# Revit family: Drinking_Fountain-Pedestal_Mounted-Murdock_Mfg-GRF_Series.rfaxxx.xxx
name_source: partatom
category: Plumbing Fixtures
units: mm (PartAtom-declared; Revit-internal decimal feet)

## family parameters
Cut with Voids When Loaded = No
Host = Face
OmniClass Number = 23.65.70.14.11
OmniClass Title = Drinking Fountains/Coolers
Part Type = Normal
Room Calculation Point = No
Round Connector Dimension = Use Diameter
Shared = Yes

## types (4) — shared parameters
-CH30 Child height, 30" bubbler height = No
-FRU1 - Underground Freeze-Resistant Valve for One Pushbutton = No
-FRU2 Freeze resistant, 2 valves = No
-FRU3 Freeze resistant, 3 valves = No
-FS Foot spray = No
-HB1 Hose bibb, compression, with hose threaded outlet/VB = No
-HB2 Hose bibb, loose key, with hose threaded outlet/VB = No
-HB3 Hose bibb, loose key, vandal resistant,  with hose threaded outlet/VB = No
-IGM In-ground 14" mounting = No
-JF1 Jug filler, spigot, self-closing valve with plain end = No
-JF2 Jug filler, pushbutton, self-closing valve with plain end = No
-NP1 Non-pollutable, freeze resistant, 1 valve = No
-NP2 Non-pollutable, freeze resistant, 2 valves = No
-NP3 Non-pollutable, freeze resistant, 3 valves = No
-PF Pet fountain receptor = No
ADA Compliant = Yes
Activation = Push Button
Assembly Code = D2010810
CW Connection = Yes
CWFU = 1.5
Cold Water Connection Diameter = 1/4"
Compliance Certifications = NSF/ANSI 61, Section 9, Public Law 111-380 (NO-LEAD), and CHSC 116875
Default Elevation = 0"
Description = Round Stainless Steel Pedestal Drinking Fountain
Finish- Bubbler = Stainless Steel-Murdock-Polished
Finish- Fountain Bowl = Stainless Steel-Murdock-18-Gauge-Type304-Grey
HW Connection = No
Height = 41 3/8"
Installation Instruction Link = https://www.murdockmfg.com
Installation Type = Pedestal Mounted
Manufacturer = Murdock Manufacturing
Product Documentation Link = https://www.murdockmfg.com
Product Page URL = https://www.murdockmfg.com
Revised Date = 02/14/2022
URL = http://www.murdockmfg.com
Vent Connection = No
WFU = 2
Warranty Documentation Link = https://www.murdockmfg.com
Waste Connection = Yes
Waste Connection Diameter = 1 1/4"
Water Pressure = 20-105 psig
Width = 12"
cUPC Compliant = Yes
zero-valued in all types: HWFU

## per-type parameters (varying)
| type | Finish | Material |
| GRF35 | Stainless_Steel-Murdock-12_Gauge-Green_Powder_Coated | Stainless_Steel-Murdock-12_Gauge-Green_Powder_Coated |
| GRF34 | Stainless_Steel-Murdock-Satin | Stainless_Steel-Murdock-Satin |
| GRF36 | Stainless_Steel-Murdock-12_Gauge-Red_Powder_Coated | Stainless_Steel-Murdock-12_Gauge-Red_Powder_Coated |
| GRF37 | Stainless_Steel-Murdock-12_Gauge-Blue_Powder_Coated | Stainless_Steel-Murdock-12_Gauge-Blue_Powder_Coated |

note: column(s) folded — value = type name in every type: Model

## geometry (parser evidence)
native form markers: Sweep x2
no freeform markers — native parametric forms only
